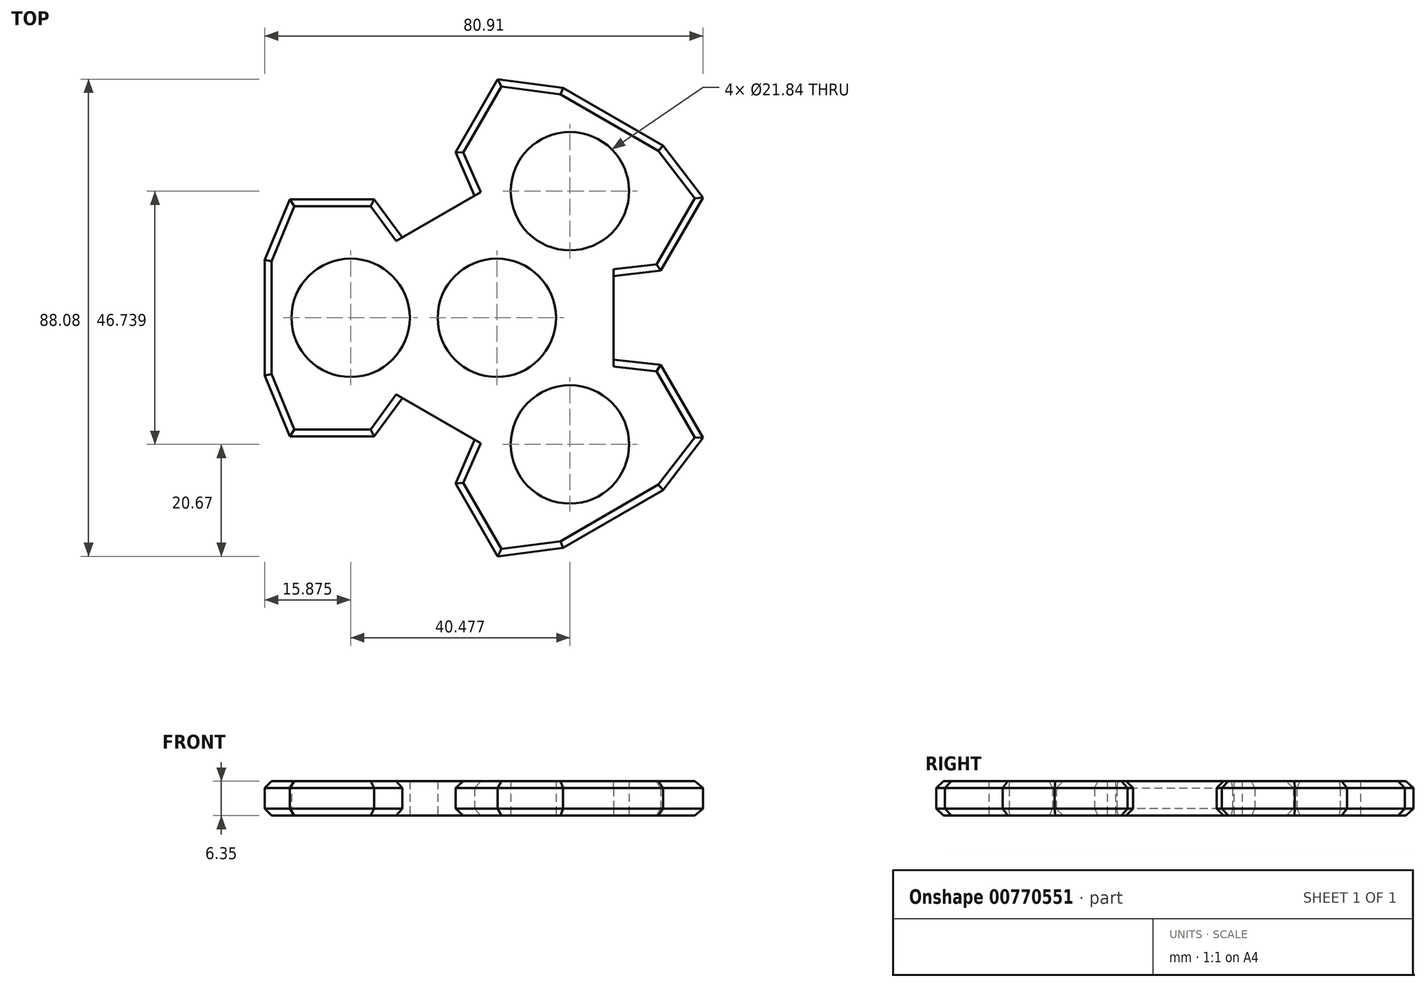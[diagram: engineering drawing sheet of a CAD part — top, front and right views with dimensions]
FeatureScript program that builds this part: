
annotation { "Feature Type Name" : "Feature", "Feature Type Description" : "" }
export const myFeature = defineFeature(function(context is Context, id is Id, definition is map)
    precondition{}
    {
        {
            var Q0;
            Q0=qCreatedBy(makeId("Top.planeOp"),FACE);
            var sketch = newSketch(context, id + "F0", { "sketchPlane" : qUnion([Q0])});
            skPoint(sketch, "E0.center", {"position": v(0, 0) * mm});
            skPoint(sketch, "E1", {"position": v(-26.98, 0) * mm});
            skPoint(sketch, "E2.1.0", {"position": v(13.5, -23.37) * mm});
            skPoint(sketch, "E2.2.0", {"position": v(13.5, 23.37) * mm});
            skLineSegment(sketch, "E3.1.2", {"start": v(21.43, -37.12) * mm, "end": v(12.19, -42.45) * mm});
            skLineSegment(sketch, "E4.2.1", {"start": v(21.43, -37.12) * mm, "end": v(30.67, -31.78) * mm});
            skLineSegment(sketch, "E5", {"start": v(21.56, -7.72) * mm, "end": v(30.27, -8.69) * mm});
            skLineSegment(sketch, "E6", {"start": v(30.27, -8.69) * mm, "end": v(38.05, -22.17) * mm});
            skLineSegment(sketch, "E7", {"start": v(38.05, -22.17) * mm, "end": v(30.67, -31.78) * mm});
            skPoint(sketch, "E8", {"position": v(21.56, -7.72) * mm});
            skPoint(sketch, "E9.MirrorP", {"position": v(21.56, 7.72) * mm});
            skLineSegment(sketch, "E10", {"start": v(21.56, 7.72) * mm, "end": v(21.56, -7.72) * mm});
            skLineSegment(sketch, "E11.MirrorCS", {"start": v(-17.46, -14.81) * mm, "end": v(-4.1, -22.53) * mm});
            skLineSegment(sketch, "E12.MirrorCS", {"start": v(-4.1, -22.53) * mm, "end": v(-7.61, -30.56) * mm});
            skLineSegment(sketch, "E13.MirrorCS", {"start": v(-7.61, -30.56) * mm, "end": v(0.17, -44.04) * mm});
            skLineSegment(sketch, "E14.MirrorCS", {"start": v(0.17, -44.04) * mm, "end": v(12.19, -42.45) * mm});
            skLineSegment(sketch, "E15.1.0", {"start": v(-17.46, 14.81) * mm, "end": v(-4.1, 22.53) * mm});
            skLineSegment(sketch, "E15.1.1", {"start": v(-4.1, 22.53) * mm, "end": v(-7.61, 30.56) * mm});
            skLineSegment(sketch, "E15.1.2", {"start": v(-7.61, 30.56) * mm, "end": v(0.17, 44.04) * mm});
            skLineSegment(sketch, "E15.1.3", {"start": v(0.17, 44.04) * mm, "end": v(12.19, 42.45) * mm});
            skLineSegment(sketch, "E15.1.4", {"start": v(21.43, 37.12) * mm, "end": v(12.19, 42.45) * mm});
            skLineSegment(sketch, "E15.1.5", {"start": v(21.43, 37.12) * mm, "end": v(30.67, 31.78) * mm});
            skLineSegment(sketch, "E15.1.6", {"start": v(38.05, 22.17) * mm, "end": v(30.67, 31.78) * mm});
            skLineSegment(sketch, "E15.1.7", {"start": v(30.27, 8.69) * mm, "end": v(38.05, 22.17) * mm});
            skLineSegment(sketch, "E15.1.8", {"start": v(21.56, 7.72) * mm, "end": v(30.27, 8.69) * mm});
            skLineSegment(sketch, "E15.1.9", {"start": v(21.56, -7.72) * mm, "end": v(21.56, 7.72) * mm});
            skLineSegment(sketch, "E15.2.0", {"start": v(-4.1, -22.53) * mm, "end": v(-17.46, -14.81) * mm});
            skLineSegment(sketch, "E15.2.1", {"start": v(-17.46, -14.81) * mm, "end": v(-22.66, -21.87) * mm});
            skLineSegment(sketch, "E15.2.2", {"start": v(-22.66, -21.87) * mm, "end": v(-38.23, -21.87) * mm});
            skLineSegment(sketch, "E15.2.3", {"start": v(-38.23, -21.87) * mm, "end": v(-42.86, -10.67) * mm});
            skLineSegment(sketch, "E15.2.4", {"start": v(-42.86, 0) * mm, "end": v(-42.86, -10.67) * mm});
            skLineSegment(sketch, "E15.2.5", {"start": v(-42.86, 0) * mm, "end": v(-42.86, 10.67) * mm});
            skLineSegment(sketch, "E15.2.6", {"start": v(-38.23, 21.87) * mm, "end": v(-42.86, 10.67) * mm});
            skLineSegment(sketch, "E15.2.7", {"start": v(-22.66, 21.87) * mm, "end": v(-38.23, 21.87) * mm});
            skLineSegment(sketch, "E15.2.8", {"start": v(-17.46, 14.81) * mm, "end": v(-22.66, 21.87) * mm});
            skLineSegment(sketch, "E15.2.9", {"start": v(-4.1, 22.53) * mm, "end": v(-17.46, 14.81) * mm});
            skSolve(sketch);
        }
        {
            var Q0;
            Q0 = qSketchRegion(id + "F0", true);
            extrude(context, id + "F1", {"entities" : qUnion([Q0]), "depth" : 6.35 * mm, "offsetDistance" : 25.4 * mm});
        }
        {
            var Q0;
            Q0=sQuery(id+"F0.wireOp",VERTEX,"E2.2.0");
            var Q1;
            Q1=sQuery(id+"F0.wireOp",VERTEX,"E0.center");
            var Q2;
            Q2=sQuery(id+"F0.wireOp",VERTEX,"E1");
            var Q3;
            Q3=sQuery(id+"F0.wireOp",VERTEX,"E2.1.0");
            var Q4;
            Q4=makeQuery(id+"F1.opExtrude","SWEPT_BODY",BODY,{"disambiguationData":[OSD([sQuery(id+"F0.wireOp",EDGE,"E3.1.2"),sQuery(id+"F0.wireOp",EDGE,"E4.2.1"),sQuery(id+"F0.wireOp",EDGE,"E5"),sQuery(id+"F0.wireOp",EDGE,"E6"),sQuery(id+"F0.wireOp",EDGE,"E7"),sQuery(id+"F0.wireOp",EDGE,"E12.MirrorCS"),sQuery(id+"F0.wireOp",EDGE,"E13.MirrorCS"),sQuery(id+"F0.wireOp",EDGE,"E14.MirrorCS"),sQuery(id+"F0.wireOp",EDGE,"E15.1.1"),sQuery(id+"F0.wireOp",EDGE,"E15.1.2"),sQuery(id+"F0.wireOp",EDGE,"E15.1.3"),sQuery(id+"F0.wireOp",EDGE,"E15.1.4"),sQuery(id+"F0.wireOp",EDGE,"E15.1.5"),sQuery(id+"F0.wireOp",EDGE,"E15.1.6"),sQuery(id+"F0.wireOp",EDGE,"E15.1.7"),sQuery(id+"F0.wireOp",EDGE,"E15.1.8"),sQuery(id+"F0.wireOp",EDGE,"E15.1.9"),sQuery(id+"F0.wireOp",EDGE,"E15.2.0"),sQuery(id+"F0.wireOp",EDGE,"E15.2.1"),sQuery(id+"F0.wireOp",EDGE,"E15.2.2"),sQuery(id+"F0.wireOp",EDGE,"E15.2.3"),sQuery(id+"F0.wireOp",EDGE,"E15.2.4"),sQuery(id+"F0.wireOp",EDGE,"E15.2.5"),sQuery(id+"F0.wireOp",EDGE,"E15.2.6"),sQuery(id+"F0.wireOp",EDGE,"E15.2.7"),sQuery(id+"F0.wireOp",EDGE,"E15.2.8"),sQuery(id+"F0.wireOp",EDGE,"E15.2.9")])]});
            hole(context, id + "F2", {"style" : HoleStyle.SIMPLE, "endStyle" : HoleEndStyle.THROUGH, "oppositeDirection" : true, "holeDiameter" : 21.84 * mm, "majorDiameter" : 6.35 * mm, "isTappedThrough" : true, "tappedDepth" : 12.7 * mm, "tapClearance" : 3, "locations" : qUnion([Q0, Q1, Q2, Q3]), "scope" : qUnion([Q4])});
        }
        {
            var Q0;
            Q0=makeQuery(id+"F1.opExtrude","CAP_EDGE",EDGE,{"disambiguationData":[OSD([sQuery(id+"F0.wireOp",EDGE,"E15.1.2")])],"isStart":true});
            var Q1;
            Q1=makeQuery(id+"F1.opExtrude","CAP_EDGE",EDGE,{"disambiguationData":[OSD([sQuery(id+"F0.wireOp",EDGE,"E15.1.2")])],"isStart":false});
            var Q2;
            Q2=makeQuery(id+"F1.opExtrude","CAP_EDGE",EDGE,{"disambiguationData":[OSD([sQuery(id+"F0.wireOp",EDGE,"E15.1.3")])],"isStart":false});
            var Q3;
            Q3=makeQuery(id+"F1.opExtrude","CAP_EDGE",EDGE,{"disambiguationData":[OSD([sQuery(id+"F0.wireOp",EDGE,"E15.1.3")])],"isStart":true});
            var Q4;
            Q4=makeQuery(id+"F1.opExtrude","CAP_EDGE",EDGE,{"disambiguationData":[OSD([sQuery(id+"F0.wireOp",EDGE,"E15.1.4"),sQuery(id+"F0.wireOp",EDGE,"E15.1.5")])],"isStart":false});
            var Q5;
            Q5=makeQuery(id+"F1.opExtrude","CAP_EDGE",EDGE,{"disambiguationData":[OSD([sQuery(id+"F0.wireOp",EDGE,"E15.1.4"),sQuery(id+"F0.wireOp",EDGE,"E15.1.5")])],"isStart":true});
            var Q6;
            Q6=makeQuery(id+"F1.opExtrude","CAP_EDGE",EDGE,{"disambiguationData":[OSD([sQuery(id+"F0.wireOp",EDGE,"E15.1.6")])],"isStart":true});
            var Q7;
            Q7=makeQuery(id+"F1.opExtrude","CAP_EDGE",EDGE,{"disambiguationData":[OSD([sQuery(id+"F0.wireOp",EDGE,"E15.1.6")])],"isStart":false});
            var Q8;
            Q8=makeQuery(id+"F1.opExtrude","CAP_EDGE",EDGE,{"disambiguationData":[OSD([sQuery(id+"F0.wireOp",EDGE,"E15.1.7")])],"isStart":true});
            var Q9;
            Q9=makeQuery(id+"F1.opExtrude","CAP_EDGE",EDGE,{"disambiguationData":[OSD([sQuery(id+"F0.wireOp",EDGE,"E15.1.7")])],"isStart":false});
            var Q10;
            Q10=makeQuery(id+"F1.opExtrude","CAP_EDGE",EDGE,{"disambiguationData":[OSD([sQuery(id+"F0.wireOp",EDGE,"E15.1.8")])],"isStart":true});
            var Q11;
            Q11=makeQuery(id+"F1.opExtrude","CAP_EDGE",EDGE,{"disambiguationData":[OSD([sQuery(id+"F0.wireOp",EDGE,"E15.1.8")])],"isStart":false});
            var Q12;
            Q12=makeQuery(id+"F1.opExtrude","CAP_EDGE",EDGE,{"disambiguationData":[OSD([sQuery(id+"F0.wireOp",EDGE,"E15.1.9")])],"isStart":true});
            var Q13;
            Q13=makeQuery(id+"F1.opExtrude","CAP_EDGE",EDGE,{"disambiguationData":[OSD([sQuery(id+"F0.wireOp",EDGE,"E15.1.9")])],"isStart":false});
            var Q14;
            Q14=makeQuery(id+"F1.opExtrude","CAP_EDGE",EDGE,{"disambiguationData":[OSD([sQuery(id+"F0.wireOp",EDGE,"E5")])],"isStart":true});
            var Q15;
            Q15=makeQuery(id+"F1.opExtrude","CAP_EDGE",EDGE,{"disambiguationData":[OSD([sQuery(id+"F0.wireOp",EDGE,"E5")])],"isStart":false});
            var Q16;
            Q16=makeQuery(id+"F1.opExtrude","CAP_EDGE",EDGE,{"disambiguationData":[OSD([sQuery(id+"F0.wireOp",EDGE,"E6")])],"isStart":true});
            var Q17;
            Q17=makeQuery(id+"F1.opExtrude","CAP_EDGE",EDGE,{"disambiguationData":[OSD([sQuery(id+"F0.wireOp",EDGE,"E6")])],"isStart":false});
            var Q18;
            Q18=makeQuery(id+"F1.opExtrude","CAP_EDGE",EDGE,{"disambiguationData":[OSD([sQuery(id+"F0.wireOp",EDGE,"E7")])],"isStart":true});
            var Q19;
            Q19=makeQuery(id+"F1.opExtrude","CAP_EDGE",EDGE,{"disambiguationData":[OSD([sQuery(id+"F0.wireOp",EDGE,"E7")])],"isStart":false});
            var Q20;
            Q20=makeQuery(id+"F1.opExtrude","CAP_EDGE",EDGE,{"disambiguationData":[OSD([sQuery(id+"F0.wireOp",EDGE,"E3.1.2"),sQuery(id+"F0.wireOp",EDGE,"E4.2.1")])],"isStart":true});
            var Q21;
            Q21=makeQuery(id+"F1.opExtrude","CAP_EDGE",EDGE,{"disambiguationData":[OSD([sQuery(id+"F0.wireOp",EDGE,"E3.1.2"),sQuery(id+"F0.wireOp",EDGE,"E4.2.1")])],"isStart":false});
            var Q22;
            Q22=makeQuery(id+"F1.opExtrude","CAP_EDGE",EDGE,{"disambiguationData":[OSD([sQuery(id+"F0.wireOp",EDGE,"E14.MirrorCS")])],"isStart":true});
            var Q23;
            Q23=makeQuery(id+"F1.opExtrude","CAP_EDGE",EDGE,{"disambiguationData":[OSD([sQuery(id+"F0.wireOp",EDGE,"E14.MirrorCS")])],"isStart":false});
            var Q24;
            Q24=makeQuery(id+"F1.opExtrude","CAP_EDGE",EDGE,{"disambiguationData":[OSD([sQuery(id+"F0.wireOp",EDGE,"E13.MirrorCS")])],"isStart":true});
            var Q25;
            Q25=makeQuery(id+"F1.opExtrude","CAP_EDGE",EDGE,{"disambiguationData":[OSD([sQuery(id+"F0.wireOp",EDGE,"E13.MirrorCS")])],"isStart":false});
            var Q26;
            Q26=makeQuery(id+"F1.opExtrude","CAP_EDGE",EDGE,{"disambiguationData":[OSD([sQuery(id+"F0.wireOp",EDGE,"E12.MirrorCS")])],"isStart":true});
            var Q27;
            Q27=makeQuery(id+"F1.opExtrude","CAP_EDGE",EDGE,{"disambiguationData":[OSD([sQuery(id+"F0.wireOp",EDGE,"E12.MirrorCS")])],"isStart":false});
            var Q28;
            Q28=makeQuery(id+"F1.opExtrude","CAP_EDGE",EDGE,{"disambiguationData":[OSD([sQuery(id+"F0.wireOp",EDGE,"E15.2.0")])],"isStart":true});
            var Q29;
            Q29=makeQuery(id+"F1.opExtrude","CAP_EDGE",EDGE,{"disambiguationData":[OSD([sQuery(id+"F0.wireOp",EDGE,"E15.2.0")])],"isStart":false});
            var Q30;
            Q30=makeQuery(id+"F1.opExtrude","CAP_EDGE",EDGE,{"disambiguationData":[OSD([sQuery(id+"F0.wireOp",EDGE,"E15.2.1")])],"isStart":false});
            var Q31;
            Q31=makeQuery(id+"F1.opExtrude","CAP_EDGE",EDGE,{"disambiguationData":[OSD([sQuery(id+"F0.wireOp",EDGE,"E15.2.1")])],"isStart":true});
            var Q32;
            Q32=makeQuery(id+"F1.opExtrude","CAP_EDGE",EDGE,{"disambiguationData":[OSD([sQuery(id+"F0.wireOp",EDGE,"E15.2.2")])],"isStart":false});
            var Q33;
            Q33=makeQuery(id+"F1.opExtrude","CAP_EDGE",EDGE,{"disambiguationData":[OSD([sQuery(id+"F0.wireOp",EDGE,"E15.2.2")])],"isStart":true});
            var Q34;
            Q34=makeQuery(id+"F1.opExtrude","CAP_EDGE",EDGE,{"disambiguationData":[OSD([sQuery(id+"F0.wireOp",EDGE,"E15.2.3")])],"isStart":false});
            var Q35;
            Q35=makeQuery(id+"F1.opExtrude","CAP_EDGE",EDGE,{"disambiguationData":[OSD([sQuery(id+"F0.wireOp",EDGE,"E15.2.3")])],"isStart":true});
            var Q36;
            Q36=makeQuery(id+"F1.opExtrude","CAP_EDGE",EDGE,{"disambiguationData":[OSD([sQuery(id+"F0.wireOp",EDGE,"E15.2.4"),sQuery(id+"F0.wireOp",EDGE,"E15.2.5")])],"isStart":false});
            var Q37;
            Q37=makeQuery(id+"F1.opExtrude","CAP_EDGE",EDGE,{"disambiguationData":[OSD([sQuery(id+"F0.wireOp",EDGE,"E15.2.4"),sQuery(id+"F0.wireOp",EDGE,"E15.2.5")])],"isStart":true});
            var Q38;
            Q38=makeQuery(id+"F1.opExtrude","CAP_EDGE",EDGE,{"disambiguationData":[OSD([sQuery(id+"F0.wireOp",EDGE,"E15.2.6")])],"isStart":false});
            var Q39;
            Q39=makeQuery(id+"F1.opExtrude","CAP_EDGE",EDGE,{"disambiguationData":[OSD([sQuery(id+"F0.wireOp",EDGE,"E15.2.6")])],"isStart":true});
            var Q40;
            Q40=makeQuery(id+"F1.opExtrude","CAP_EDGE",EDGE,{"disambiguationData":[OSD([sQuery(id+"F0.wireOp",EDGE,"E15.2.7")])],"isStart":false});
            var Q41;
            Q41=makeQuery(id+"F1.opExtrude","CAP_EDGE",EDGE,{"disambiguationData":[OSD([sQuery(id+"F0.wireOp",EDGE,"E15.2.7")])],"isStart":true});
            var Q42;
            Q42=makeQuery(id+"F1.opExtrude","CAP_EDGE",EDGE,{"disambiguationData":[OSD([sQuery(id+"F0.wireOp",EDGE,"E15.2.8")])],"isStart":false});
            var Q43;
            Q43=makeQuery(id+"F1.opExtrude","CAP_EDGE",EDGE,{"disambiguationData":[OSD([sQuery(id+"F0.wireOp",EDGE,"E15.2.8")])],"isStart":true});
            var Q44;
            Q44=makeQuery(id+"F1.opExtrude","CAP_EDGE",EDGE,{"disambiguationData":[OSD([sQuery(id+"F0.wireOp",EDGE,"E15.2.9")])],"isStart":false});
            var Q45;
            Q45=makeQuery(id+"F1.opExtrude","CAP_EDGE",EDGE,{"disambiguationData":[OSD([sQuery(id+"F0.wireOp",EDGE,"E15.2.9")])],"isStart":true});
            var Q46;
            Q46=makeQuery(id+"F1.opExtrude","CAP_EDGE",EDGE,{"disambiguationData":[OSD([sQuery(id+"F0.wireOp",EDGE,"E15.1.1")])],"isStart":true});
            var Q47;
            Q47=makeQuery(id+"F1.opExtrude","CAP_EDGE",EDGE,{"disambiguationData":[OSD([sQuery(id+"F0.wireOp",EDGE,"E15.1.1")])],"isStart":false});
            chamfer(context, id + "F3", {"entities" : qUnion([Q0, Q1, Q2, Q3, Q4, Q5, Q6, Q7, Q8, Q9, Q10, Q11, Q12, Q13, Q14, Q15, Q16, Q17, Q18, Q19, Q20, Q21, Q22, Q23, Q24, Q25, Q26, Q27, Q28, Q29, Q30, Q31, Q32, Q33, Q34, Q35, Q36, Q37, Q38, Q39, Q40, Q41, Q42, Q43, Q44, Q45, Q46, Q47]), "width" : 1.27 * mm, "tangentPropagation" : true});
        }
    });
